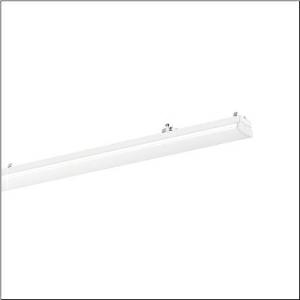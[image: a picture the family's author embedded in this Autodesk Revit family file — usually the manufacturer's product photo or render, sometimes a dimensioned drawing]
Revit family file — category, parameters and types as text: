
# Revit family: licross_11_recessed_opal_ho_51te1ddv4m1m
name_source: partatom
category: Lighting Fixtures
units: mm (PartAtom-declared; Revit-internal decimal feet)

## family parameters
Cut with Voids When Loaded = No
Host = Face
Light Source = No
Part Type = Normal
Room Calculation Point = No
Round Connector Dimension = Use Diameter
Shared = No

## types (1)
- --- (1 x LED, 26350 lm, 150.5 W, 4000K)
    Apparent Load = 150 VA
    CIE Flux Codes = 44 73 91 87 100
    Color Rendering = 80
    Color Temperature = 4000K
    Default Elevation = 1800 mm
    Description = Licross 11 recessed opal HO, luminaire insert, of sheet steel, coil coated, white, length: 2.250mm, width: 76mm, height: 87mm, LED rated luminous flux: 26.350lm, light colour: 840, SDCM (Standard Deviation of Colour Matching)MacAdam ≤ 2 SDCM (initial), control gear: DALI 2, with plug, 5-pole, with phase selection, mains connection: 220..240V, AC, 50/60Hz, rated input power: 151W, internal wiring halogen-free, primary optical cover: cover, of PMMA, light emission: direct with ceiling illumination distribution, primary light characteristic: symmetric, protection rating (complete): IP54, insulation class (complete): insulation class I (protective earthing), certification: CE, ENEC, VDE, UKCA, protection symbol: D if used in an environment with non-conductive dust loads with corresponding accessories, impact resistance: IK06, permissible ambient temperature for indoor applications: -40..+35°C, corresponds to IFS (International Featured Standards) requirements for safety and quality in the food industry, reducing of maximum allowable ambient temperature of 5°C with ceiling mounting, LABS conformity tested according to VDMA 24364:2018-05, The light source and the operating device comply with the requirements of the Ecodesign Regulation (EU) 2019/2020 and are replaceable in accordance with this regulation, packaging unit: 1 piece
    Height = 83 mm
    Lamp = 1 x LED
    Lamp Light Flux = 26350 lm
    Lamp Power = 150.5 W
    Lamp count = 1
    Length = 2250 mm
    Luminous efficacy = 175 lm/W
    Manufacturer = Siteco
    ModVariant = No
    Model = 51TE1DDV4M1M
    Mounting Place = Ceiling
    Mounting Type = Pendant
    Number of Poles = 1
    OnlyDefault = Yes
    Power Factor = 1
    Product Name = Licross 11 recessed opal HO
    Product group = luminaire insert | ceiling pendant
    ProductGroupID = 901
    Protection Class = Protection class I
    Protection Degree = IP 54
    RLX_Detail_Level = 1
    RLX_Emergency_Light_Flux = 0 lm
    RLX_Emergency_Type = 0
    RLX_Emergency_Type_DB = No
    RlxData = <blob elided: 27309 chars, md5=1a0f4320>
    Socket = socket
    Standby Power = 0 W
    System Light Flux = 26350 lm
    System Power = 150 W
    Type Comments = factory setting: luminous flux: 100 % | dim-lin: 254 | 690 mA
    Type Image = l_1313666.jpg
    URL = http://relux.com
    VarID = @adj_084045
    Voltage = 0 V
    Weight = 0.00 kg
    Width = 76 mm

## geometry (parser evidence)
native form markers: Blend x4, Sweep x12
no freeform markers — native parametric forms only
